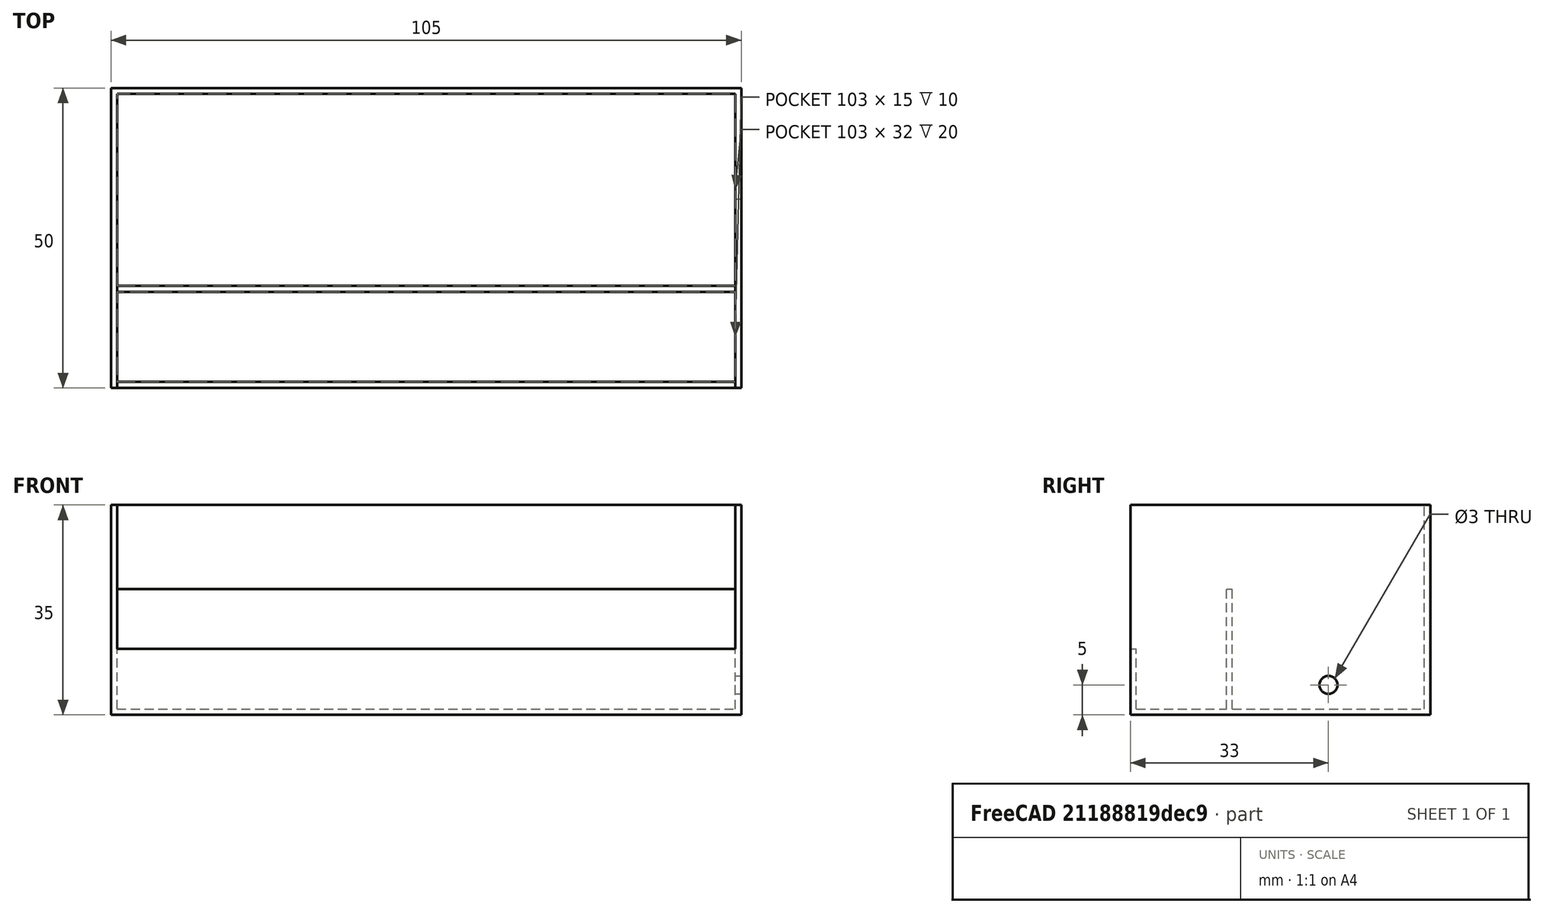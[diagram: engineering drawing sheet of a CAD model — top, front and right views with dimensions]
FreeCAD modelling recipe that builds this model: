
FCSTD DOCUMENT  (FreeCAD 0.19R24267 +99 (Git))
Label: infinityPool
License: All rights reserved
LicenseURL: http://en.wikipedia.org/wiki/All_rights_reserved
objects: Part::Box×4, Part::Cut×2, Part::MultiFuse×1, Part::Cylinder×1
note: 8 computed .brp shape members not serialized (recipe doc carries the construction recipe); baked Part::Feature solids carry a one-line shape summary decoded from their .brp

FEATURE [Part::Box] Box  label="Bounding Box"
  AttacherType = Attacher::AttachEngine3D
  Height = 35
  Length = 105
  Width = 50
FEATURE [Part::Box] Box001  label="Primary Cut Out"
  AttacherType = Attacher::AttachEngine3D
  Height = 34
  Length = 103
  Placement = pos=(1,0,1) rot=(0,0,1;0rad)
  Width = 49
FEATURE [Part::Cut] Cut
  Base = -> Box
  Tool = -> Box001
FEATURE [Part::Box] Box002  label="Front Piece"
  AttacherType = Attacher::AttachEngine3D
  Height = 10
  Length = 103
  Placement = pos=(1,0,1) rot=(0,0,1;0rad)
  Width = 1
FEATURE [Part::Box] Box003  label="Mid Piece"
  AttacherType = Attacher::AttachEngine3D
  Height = 20
  Length = 103
  Placement = pos=(1,16,1) rot=(0,0,1;0rad)
  Width = 1
FEATURE [Part::MultiFuse] Fusion
  Shapes = -> [Cut,Box002,Box003]
FEATURE [Part::Cylinder] Cylinder  label="Pump Hole"
  Angle = 360
  AttacherType = Attacher::AttachEngine3D
  Height = 10
  Placement = pos=(100,33,5) rot=(0,1,0;1.5708rad)
  Radius = 1.5
FEATURE [Part::Cut] Cut001  label="Pool"
  Base = -> Fusion
  Placement = pos=(2,0,0) rot=(0,0,1;0rad)
  Tool = -> Cylinder
